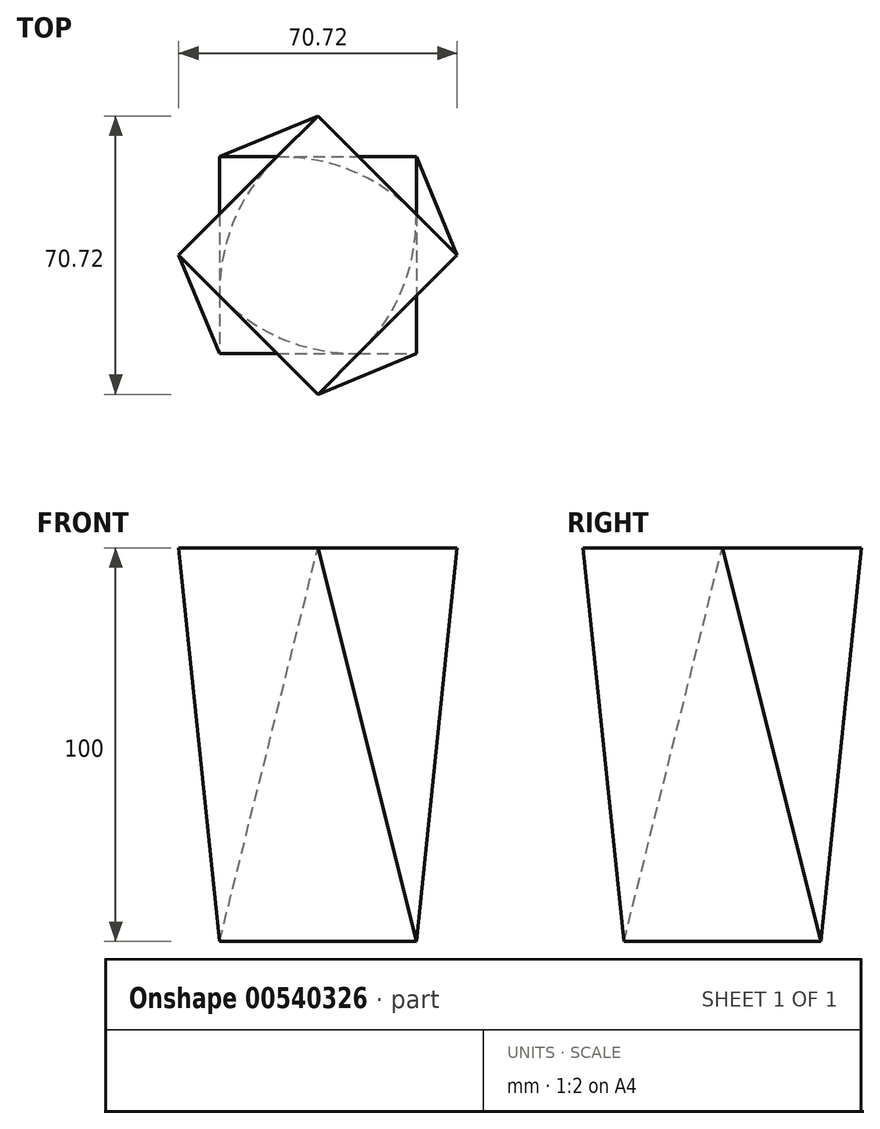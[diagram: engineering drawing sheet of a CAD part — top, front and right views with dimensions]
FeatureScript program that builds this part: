
annotation { "Feature Type Name" : "Feature", "Feature Type Description" : "" }
export const myFeature = defineFeature(function(context is Context, id is Id, definition is map)
    precondition{}
    {
        {
            var Q0;
            Q0=qCreatedBy(makeId("Top.planeOp"),FACE);
            var sketch = newSketch(context, id + "F0", { "sketchPlane" : qUnion([Q0])});
            skLineSegment(sketch, "E0.bottom", {"start": v(-25, 25) * mm, "end": v(25, 25) * mm});
            skLineSegment(sketch, "E0.top", {"start": v(-25, -25) * mm, "end": v(25, -25) * mm});
            skLineSegment(sketch, "E0.left", {"start": v(-25, 25) * mm, "end": v(-25, -25) * mm});
            skLineSegment(sketch, "E0.right", {"start": v(25, 25) * mm, "end": v(25, -25) * mm});
            skPoint(sketch, "E0.middle", {"position": v(0, 0) * mm});
            skSolve(sketch);
        }
        {
            var Q0;
            Q0=qCreatedBy(makeId("Top.planeOp"),FACE);
            cPlane(context, id + "F1", {"entities" : qUnion([Q0]), "cplaneType" : CPlaneType.OFFSET, "offset" : 100 * mm, "width" : 150 * mm, "height" : 150 * mm});
        }
        {
            var Q0;
            Q0=qCreatedBy(id+"F1.planeOp",FACE);
            var sketch = newSketch(context, id + "F2", { "sketchPlane" : qUnion([Q0])});
            skLineSegment(sketch, "E1.bottom", {"start": v(-35.36, 0) * mm, "end": v(0, 35.36) * mm});
            skLineSegment(sketch, "E1.top", {"start": v(0, -35.36) * mm, "end": v(35.36, 0) * mm});
            skLineSegment(sketch, "E1.left", {"start": v(-35.36, 0) * mm, "end": v(0, -35.36) * mm});
            skLineSegment(sketch, "E1.right", {"start": v(0, 35.36) * mm, "end": v(35.36, 0) * mm});
            skPoint(sketch, "E1.middle", {"position": v(0, 0) * mm});
            skSolve(sketch);
        }
        {
            var Q0;
            Q0=makeQuery(id+"F0.imprint","IMPRINT",FACE,{"disambiguationData":[TD([[makeQuery(id+"F0.imprint","IMPRINT",EDGE,{"derivedFrom":sQuery(id+"F0.wireOp",EDGE,"E0.bottom")}),-1.0]])]});
            var Q1;
            Q1=makeQuery(id+"F2.imprint","IMPRINT",FACE,{"disambiguationData":[TD([[makeQuery(id+"F2.imprint","IMPRINT",EDGE,{"derivedFrom":sQuery(id+"F2.wireOp",EDGE,"E1.bottom")}),-1.0]])]});
            loft(context, id + "F3", {"sheetProfilesArray" : [{ "sheetProfileEntities" : qUnion([Q0]) }, { "sheetProfileEntities" : qUnion([Q1]) }]});
        }
    });
